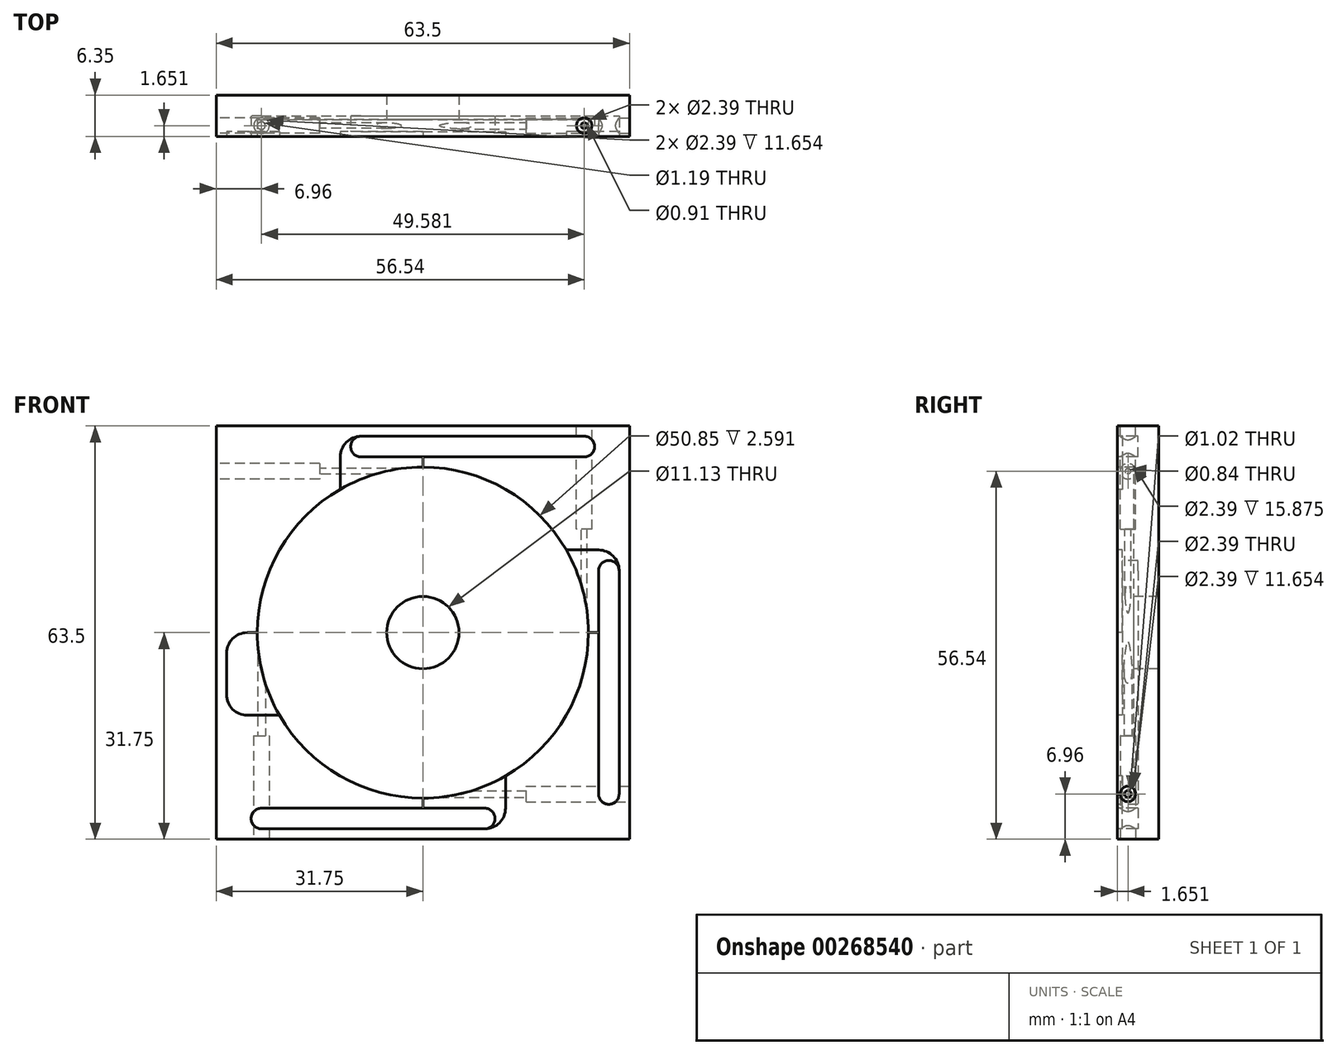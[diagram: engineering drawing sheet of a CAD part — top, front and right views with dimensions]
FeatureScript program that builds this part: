
annotation { "Feature Type Name" : "Feature", "Feature Type Description" : "" }
export const myFeature = defineFeature(function(context is Context, id is Id, definition is map)
    precondition{}
    {
        {
            var Q0;
            Q0=qCreatedBy(makeId("Front.planeOp"),FACE);
            var sketch = newSketch(context, id + "F0", { "sketchPlane" : qUnion([Q0])});
            skLineSegment(sketch, "E0.bottom", {"start": v(-31.75, 31.75) * mm, "end": v(31.75, 31.75) * mm});
            skLineSegment(sketch, "E0.top", {"start": v(-31.75, -31.75) * mm, "end": v(31.75, -31.75) * mm});
            skLineSegment(sketch, "E0.left", {"start": v(-31.75, 31.75) * mm, "end": v(-31.75, -31.75) * mm});
            skLineSegment(sketch, "E0.right", {"start": v(31.75, 31.75) * mm, "end": v(31.75, -31.75) * mm});
            skCircle(sketch, "E1", {"center": v(0, 0) * mm, "radius": 5.56 * mm});
            skSolve(sketch);
        }
        {
            var Q0;
            Q0 = qSketchRegion(id + "F0", true);
            extrude(context, id + "F1", {"entities" : qUnion([Q0]), "oppositeDirection" : true, "depth" : 6.35 * mm, "offsetDistance" : 25.4 * mm});
        }
        {
            var Q0;
            Q0=makeQuery(id+"F1.opExtrude","CAP_FACE",FACE,{"disambiguationData":[OSD([sQuery(id+"F0.wireOp",EDGE,"E0.bottom"),sQuery(id+"F0.wireOp",EDGE,"E0.top"),sQuery(id+"F0.wireOp",EDGE,"E0.left"),sQuery(id+"F0.wireOp",EDGE,"E0.right"),sQuery(id+"F0.wireOp",EDGE,"E1")])],"isStart":true});
            var sketch = newSketch(context, id + "F2", { "sketchPlane" : qUnion([Q0])});
            skCircle(sketch, "E2", {"center": v(0, 0) * mm, "radius": 25.43 * mm});
            skSolve(sketch);
        }
        {
            var Q0;
            Q0 = qSketchRegion(id + "F2", true);
            extrude(context, id + "F3", {"entities" : qUnion([Q0]), "operationType" : NewBodyOperationType.REMOVE, "oppositeDirection" : true, "depth" : 2.6 * mm, "offsetDistance" : 25.4 * mm});
        }
        {
            var Q0;
            Q0=makeQuery(id+"F1.opExtrude","SWEPT_FACE",FACE,{"disambiguationData":[OSD([sQuery(id+"F0.wireOp",EDGE,"E0.left")])]});
            var sketch = newSketch(context, id + "F4", { "sketchPlane" : qUnion([Q0])});
            skCircle(sketch, "E3", {"center": v(-1.65, 24.8) * mm, "radius": 0.42 * mm});
            skSolve(sketch);
        }
        {
            var Q0;
            Q0 = qSketchRegion(id + "F4", true);
            extrude(context, id + "F5", {"entities" : qUnion([Q0]), "operationType" : NewBodyOperationType.REMOVE, "oppositeDirection" : true, "depth" : 31.75 * mm, "offsetDistance" : 25.4 * mm});
        }
        {
            var Q0;
            Q0=makeQuery(id+"F1.opExtrude","SWEPT_FACE",FACE,{"disambiguationData":[OSD([sQuery(id+"F0.wireOp",EDGE,"E0.top")])]});
            var sketch = newSketch(context, id + "F6", { "sketchPlane" : qUnion([Q0])});
            skCircle(sketch, "E4", {"center": v(-24.8, -1.65) * mm, "radius": 0.6 * mm});
            skSolve(sketch);
        }
        {
            var Q0;
            Q0 = qSketchRegion(id + "F6", true);
            extrude(context, id + "F7", {"entities" : qUnion([Q0]), "operationType" : NewBodyOperationType.REMOVE, "oppositeDirection" : true, "depth" : 31.75 * mm, "offsetDistance" : 25.4 * mm});
        }
        {
            var Q0;
            Q0=makeQuery(id+"F1.opExtrude","SWEPT_FACE",FACE,{"disambiguationData":[OSD([sQuery(id+"F0.wireOp",EDGE,"E0.bottom")])]});
            var sketch = newSketch(context, id + "F8", { "sketchPlane" : qUnion([Q0])});
            skCircle(sketch, "E5", {"center": v(24.8, 1.65) * mm, "radius": 0.46 * mm});
            skSolve(sketch);
        }
        {
            var Q0;
            Q0 = qSketchRegion(id + "F8", true);
            extrude(context, id + "F9", {"entities" : qUnion([Q0]), "operationType" : NewBodyOperationType.REMOVE, "oppositeDirection" : true, "depth" : 31.75 * mm, "offsetDistance" : 25.4 * mm});
        }
        {
            var Q0;
            Q0=makeQuery(id+"F1.opExtrude","SWEPT_FACE",FACE,{"disambiguationData":[OSD([sQuery(id+"F0.wireOp",EDGE,"E0.right")])]});
            var sketch = newSketch(context, id + "F10", { "sketchPlane" : qUnion([Q0])});
            skCircle(sketch, "E6", {"center": v(1.65, -24.8) * mm, "radius": 0.5 * mm});
            skSolve(sketch);
        }
        {
            var Q0;
            Q0 = qSketchRegion(id + "F10", true);
            var Q1;
            Q1=makeQuery(id+"F1.opExtrude","SWEPT_FACE",FACE,{"disambiguationData":[OSD([sQuery(id+"F0.wireOp",EDGE,"E0.left")])]});
            extrude(context, id + "F11", {"entities" : qUnion([Q0, Q1]), "operationType" : NewBodyOperationType.REMOVE, "oppositeDirection" : true, "depth" : 31.75 * mm, "offsetDistance" : 25.4 * mm});
        }
        {
            var Q0;
            Q0=makeQuery(id+"F1.opExtrude","CAP_FACE",FACE,{"disambiguationData":[OSD([sQuery(id+"F0.wireOp",EDGE,"E0.bottom"),sQuery(id+"F0.wireOp",EDGE,"E0.top"),sQuery(id+"F0.wireOp",EDGE,"E0.left"),sQuery(id+"F0.wireOp",EDGE,"E0.right"),sQuery(id+"F0.wireOp",EDGE,"E1")])],"isStart":true});
            var sketch = newSketch(context, id + "F12", { "sketchPlane" : qUnion([Q0])});
            skArc(sketch, "E7", {"start": v(-9.53, 30.16) * mm, "mid": v(-11.77, 29.23) * mm, "end": v(-12.7, 26.99) * mm});
            skArc(sketch, "E8", {"start": v(30.16, 9.53) * mm, "mid": v(29.23, 11.77) * mm, "end": v(26.99, 12.7) * mm});
            skArc(sketch, "E9", {"start": v(9.53, -30.16) * mm, "mid": v(11.77, -29.23) * mm, "end": v(12.7, -26.99) * mm});
            skArc(sketch, "E10", {"start": v(-26.99, -6.35) * mm, "mid": v(-30.16, -9.53) * mm, "end": v(-26.99, -12.7) * mm});
            skLineSegment(sketch, "E11", {"start": v(26.99, 12.7) * mm, "end": v(19.5, 12.7) * mm});
            skLineSegment(sketch, "E12", {"start": v(19.5, 12.7) * mm, "end": v(19.5, 6.35) * mm});
            skLineSegment(sketch, "E13", {"start": v(19.5, 6.35) * mm, "end": v(26.99, 6.35) * mm});
            skLineSegment(sketch, "E14", {"start": v(6.35, -26.99) * mm, "end": v(6.35, -18.32) * mm});
            skLineSegment(sketch, "E15", {"start": v(6.35, -18.32) * mm, "end": v(12.7, -18.32) * mm});
            skLineSegment(sketch, "E16", {"start": v(12.7, -18.32) * mm, "end": v(12.7, -26.99) * mm});
            skLineSegment(sketch, "E17", {"start": v(-26.99, -6.35) * mm, "end": v(-17.38, -6.35) * mm});
            skLineSegment(sketch, "E18", {"start": v(-17.38, -6.35) * mm, "end": v(-17.38, -12.7) * mm});
            skLineSegment(sketch, "E19", {"start": v(-17.38, -12.7) * mm, "end": v(-26.99, -12.7) * mm});
            skLineSegment(sketch, "E20", {"start": v(-12.7, 26.99) * mm, "end": v(-12.7, 19.16) * mm});
            skLineSegment(sketch, "E21", {"start": v(-12.7, 19.16) * mm, "end": v(-6.35, 19.16) * mm});
            skLineSegment(sketch, "E22", {"start": v(-6.35, 19.16) * mm, "end": v(-6.35, 26.99) * mm});
            skArc(sketch, "E23", {"start": v(24.8, 26.99) * mm, "mid": v(26.38, 28.58) * mm, "end": v(24.8, 30.16) * mm});
            skLineSegment(sketch, "E24", {"start": v(24.8, 30.16) * mm, "end": v(-9.53, 30.16) * mm});
            skLineSegment(sketch, "E25", {"start": v(24.8, 26.99) * mm, "end": v(-6.35, 26.99) * mm});
            skArc(sketch, "E26", {"start": v(26.99, -24.8) * mm, "mid": v(28.58, -26.38) * mm, "end": v(30.16, -24.8) * mm});
            skLineSegment(sketch, "E27", {"start": v(26.99, 6.35) * mm, "end": v(26.99, -24.8) * mm});
            skLineSegment(sketch, "E28", {"start": v(30.16, -24.8) * mm, "end": v(30.16, 9.53) * mm});
            skPoint(sketch, "E28.endSnap0", {"position": v(30.16, 9.53) * mm});
            skArc(sketch, "E29", {"start": v(-24.8, -26.99) * mm, "mid": v(-26.38, -28.58) * mm, "end": v(-24.8, -30.16) * mm});
            skLineSegment(sketch, "E30", {"start": v(-24.8, -30.16) * mm, "end": v(9.53, -30.16) * mm});
            skLineSegment(sketch, "E31", {"start": v(-24.8, -26.99) * mm, "end": v(6.35, -26.99) * mm});
            skSolve(sketch);
        }
        {
            var Q0;
            Q0 = qSketchRegion(id + "F12", true);
            extrude(context, id + "F13", {"entities" : qUnion([Q0]), "operationType" : NewBodyOperationType.REMOVE, "oppositeDirection" : true, "depth" : 0.76 * mm, "offsetDistance" : 25.4 * mm});
        }
        {
            var Q0;
            Q0=makeQuery(id+"F1.opExtrude","CAP_FACE",FACE,{"disambiguationData":[OSD([sQuery(id+"F0.wireOp",EDGE,"E0.bottom"),sQuery(id+"F0.wireOp",EDGE,"E0.top"),sQuery(id+"F0.wireOp",EDGE,"E0.left"),sQuery(id+"F0.wireOp",EDGE,"E0.right"),sQuery(id+"F0.wireOp",EDGE,"E1")])],"isStart":true});
            var sketch = newSketch(context, id + "F14", { "sketchPlane" : qUnion([Q0])});
            skCircle(sketch, "E32", {"center": v(-24.76, -28.57) * mm, "radius": 1.59 * mm});
            skCircle(sketch, "E33", {"center": v(24.8, 28.58) * mm, "radius": 1.59 * mm});
            skCircle(sketch, "E34", {"center": v(28.58, -24.8) * mm, "radius": 1.59 * mm});
            skSolve(sketch);
        }
        {
            var Q0;
            Q0 = qSketchRegion(id + "F14", true);
            extrude(context, id + "F15", {"entities" : qUnion([Q0]), "operationType" : NewBodyOperationType.REMOVE, "oppositeDirection" : true, "depth" : 3.17 * mm, "offsetDistance" : 25.4 * mm});
        }
        {
            var Q0;
            Q0=makeQuery(id+"F1.opExtrude","CAP_FACE",FACE,{"disambiguationData":[OSD([sQuery(id+"F0.wireOp",EDGE,"E0.bottom"),sQuery(id+"F0.wireOp",EDGE,"E0.top"),sQuery(id+"F0.wireOp",EDGE,"E0.left"),sQuery(id+"F0.wireOp",EDGE,"E0.right"),sQuery(id+"F0.wireOp",EDGE,"E1")])],"isStart":true});
            var sketch = newSketch(context, id + "F16", { "sketchPlane" : qUnion([Q0])});
            skLineSegment(sketch, "E35.bottom", {"start": v(-6.35, 26.99) * mm, "end": v(0, 26.99) * mm});
            skLineSegment(sketch, "E35.top", {"start": v(-6.35, 22.16) * mm, "end": v(0, 22.16) * mm});
            skLineSegment(sketch, "E35.left", {"start": v(-6.35, 26.99) * mm, "end": v(-6.35, 22.16) * mm});
            skLineSegment(sketch, "E35.right", {"start": v(0, 26.99) * mm, "end": v(0, 22.16) * mm});
            skLineSegment(sketch, "E36.bottom", {"start": v(16.43, 6.35) * mm, "end": v(26.99, 6.35) * mm});
            skLineSegment(sketch, "E36.top", {"start": v(16.43, 0) * mm, "end": v(26.99, 0) * mm});
            skLineSegment(sketch, "E36.left", {"start": v(16.43, 6.35) * mm, "end": v(16.43, 0) * mm});
            skLineSegment(sketch, "E36.right", {"start": v(26.99, 6.35) * mm, "end": v(26.99, 0) * mm});
            skLineSegment(sketch, "E37.bottom", {"start": v(6.35, -26.99) * mm, "end": v(0, -26.99) * mm});
            skLineSegment(sketch, "E37.top", {"start": v(6.35, -17.51) * mm, "end": v(0, -17.51) * mm});
            skLineSegment(sketch, "E37.left", {"start": v(6.35, -26.99) * mm, "end": v(6.35, -17.51) * mm});
            skLineSegment(sketch, "E37.right", {"start": v(0, -26.99) * mm, "end": v(0, -17.51) * mm});
            skArc(sketch, "E38", {"start": v(-26.99, 0) * mm, "mid": v(-29.23, -0.93) * mm, "end": v(-30.16, -3.18) * mm});
            skArc(sketch, "E39.0", {"start": v(-26.99, -6.35) * mm, "mid": v(-29.23, -7.28) * mm, "end": v(-30.16, -9.53) * mm});
            skLineSegment(sketch, "E40.0", {"start": v(-26.99, -6.35) * mm, "end": v(-24.62, -6.35) * mm});
            skLineSegment(sketch, "E41", {"start": v(-30.16, -9.53) * mm, "end": v(-30.16, -3.18) * mm});
            skLineSegment(sketch, "E42", {"start": v(-26.99, 0) * mm, "end": v(-25.43, 0) * mm});
            skArc(sketch, "E43.0", {"start": v(-25.43, 0) * mm, "mid": v(-25.22, -3.2) * mm, "end": v(-24.62, -6.35) * mm});
            skPoint(sketch, "E44.orphan", {"position": v(-12.7, 22.03) * mm});
            skSolve(sketch);
        }
        {
            var Q0;
            Q0 = qSketchRegion(id + "F16", true);
            extrude(context, id + "F17", {"entities" : qUnion([Q0]), "operationType" : NewBodyOperationType.REMOVE, "oppositeDirection" : true, "depth" : 0.76 * mm, "offsetDistance" : 25.4 * mm});
        }
        {
            var Q0;
            Q0=makeQuery(id+"F1.opExtrude","CAP_FACE",FACE,{"disambiguationData":[OSD([sQuery(id+"F0.wireOp",EDGE,"E0.bottom"),sQuery(id+"F0.wireOp",EDGE,"E0.top"),sQuery(id+"F0.wireOp",EDGE,"E0.left"),sQuery(id+"F0.wireOp",EDGE,"E0.right"),sQuery(id+"F0.wireOp",EDGE,"E1")])],"isStart":true});
            var sketch = newSketch(context, id + "F18", { "sketchPlane" : qUnion([Q0])});
            skPoint(sketch, "E45.centerSnap0", {"position": v(26.38, 22.98) * mm});
            skArc(sketch, "E46", {"start": v(-9.5, 30.16) * mm, "mid": v(-11.09, 28.58) * mm, "end": v(-9.5, 26.99) * mm});
            skArc(sketch, "E47", {"start": v(24.8, 26.99) * mm, "mid": v(26.38, 28.58) * mm, "end": v(24.8, 30.16) * mm});
            skLineSegment(sketch, "E48", {"start": v(-9.5, 30.16) * mm, "end": v(24.8, 30.16) * mm});
            skLineSegment(sketch, "E49", {"start": v(-9.5, 26.99) * mm, "end": v(24.8, 26.99) * mm});
            skArc(sketch, "E50", {"start": v(26.99, -24.8) * mm, "mid": v(28.58, -26.38) * mm, "end": v(30.16, -24.8) * mm});
            skArc(sketch, "E51", {"start": v(30.16, 9.5) * mm, "mid": v(28.57, 11.09) * mm, "end": v(26.99, 9.5) * mm});
            skLineSegment(sketch, "E52", {"start": v(26.99, 9.5) * mm, "end": v(26.99, -24.8) * mm});
            skLineSegment(sketch, "E53", {"start": v(30.16, 9.5) * mm, "end": v(30.16, -24.8) * mm});
            skArc(sketch, "E54", {"start": v(-24.8, -26.99) * mm, "mid": v(-26.38, -28.58) * mm, "end": v(-24.8, -30.16) * mm});
            skArc(sketch, "E55", {"start": v(9.5, -30.16) * mm, "mid": v(11.09, -28.57) * mm, "end": v(9.5, -26.99) * mm});
            skLineSegment(sketch, "E56", {"start": v(-24.8, -26.99) * mm, "end": v(9.5, -26.99) * mm});
            skLineSegment(sketch, "E57", {"start": v(-24.8, -30.16) * mm, "end": v(9.5, -30.16) * mm});
            skSolve(sketch);
        }
        {
            var Q0;
            Q0 = qSketchRegion(id + "F18", true);
            extrude(context, id + "F19", {"entities" : qUnion([Q0]), "operationType" : NewBodyOperationType.REMOVE, "oppositeDirection" : true, "depth" : 3.17 * mm, "offsetDistance" : 25.4 * mm});
        }
        {
            var Q0;
            Q0=makeQuery(id+"F1.opExtrude","SWEPT_FACE",FACE,{"disambiguationData":[OSD([sQuery(id+"F0.wireOp",EDGE,"E0.left")])]});
            var sketch = newSketch(context, id + "F20", { "sketchPlane" : qUnion([Q0])});
            skCircle(sketch, "E58", {"center": v(-1.65, 24.8) * mm, "radius": 1.2 * mm});
            skSolve(sketch);
        }
        {
            var Q0;
            Q0 = qSketchRegion(id + "F20", true);
            extrude(context, id + "F21", {"entities" : qUnion([Q0]), "operationType" : NewBodyOperationType.REMOVE, "oppositeDirection" : true, "depth" : 15.88 * mm, "offsetDistance" : 25.4 * mm});
        }
        {
            var Q0;
            Q0=makeQuery(id+"F1.opExtrude","SWEPT_FACE",FACE,{"disambiguationData":[OSD([sQuery(id+"F0.wireOp",EDGE,"E0.bottom")])]});
            var sketch = newSketch(context, id + "F22", { "sketchPlane" : qUnion([Q0])});
            skCircle(sketch, "E59", {"center": v(24.8, 1.65) * mm, "radius": 1.2 * mm});
            skSolve(sketch);
        }
        {
            var Q0;
            Q0 = qSketchRegion(id + "F22", true);
            extrude(context, id + "F23", {"entities" : qUnion([Q0]), "operationType" : NewBodyOperationType.REMOVE, "oppositeDirection" : true, "depth" : 15.88 * mm, "offsetDistance" : 25.4 * mm});
        }
        {
            var Q0;
            Q0=makeQuery(id+"F1.opExtrude","SWEPT_FACE",FACE,{"disambiguationData":[OSD([sQuery(id+"F0.wireOp",EDGE,"E0.right")])]});
            var sketch = newSketch(context, id + "F24", { "sketchPlane" : qUnion([Q0])});
            skCircle(sketch, "E60", {"center": v(1.65, -24.8) * mm, "radius": 1.2 * mm});
            skSolve(sketch);
        }
        {
            var Q0;
            Q0 = qSketchRegion(id + "F24", true);
            extrude(context, id + "F25", {"entities" : qUnion([Q0]), "operationType" : NewBodyOperationType.REMOVE, "oppositeDirection" : true, "depth" : 15.88 * mm, "offsetDistance" : 25.4 * mm});
        }
        {
            var Q0;
            Q0=makeQuery(id+"F1.opExtrude","SWEPT_FACE",FACE,{"disambiguationData":[OSD([sQuery(id+"F0.wireOp",EDGE,"E0.top")])]});
            var sketch = newSketch(context, id + "F26", { "sketchPlane" : qUnion([Q0])});
            skCircle(sketch, "E61", {"center": v(-24.8, -1.65) * mm, "radius": 1.2 * mm});
            skSolve(sketch);
        }
        {
            var Q0;
            Q0 = qSketchRegion(id + "F26", true);
            extrude(context, id + "F27", {"entities" : qUnion([Q0]), "operationType" : NewBodyOperationType.REMOVE, "oppositeDirection" : true, "depth" : 15.88 * mm, "offsetDistance" : 25.4 * mm});
        }
    });
